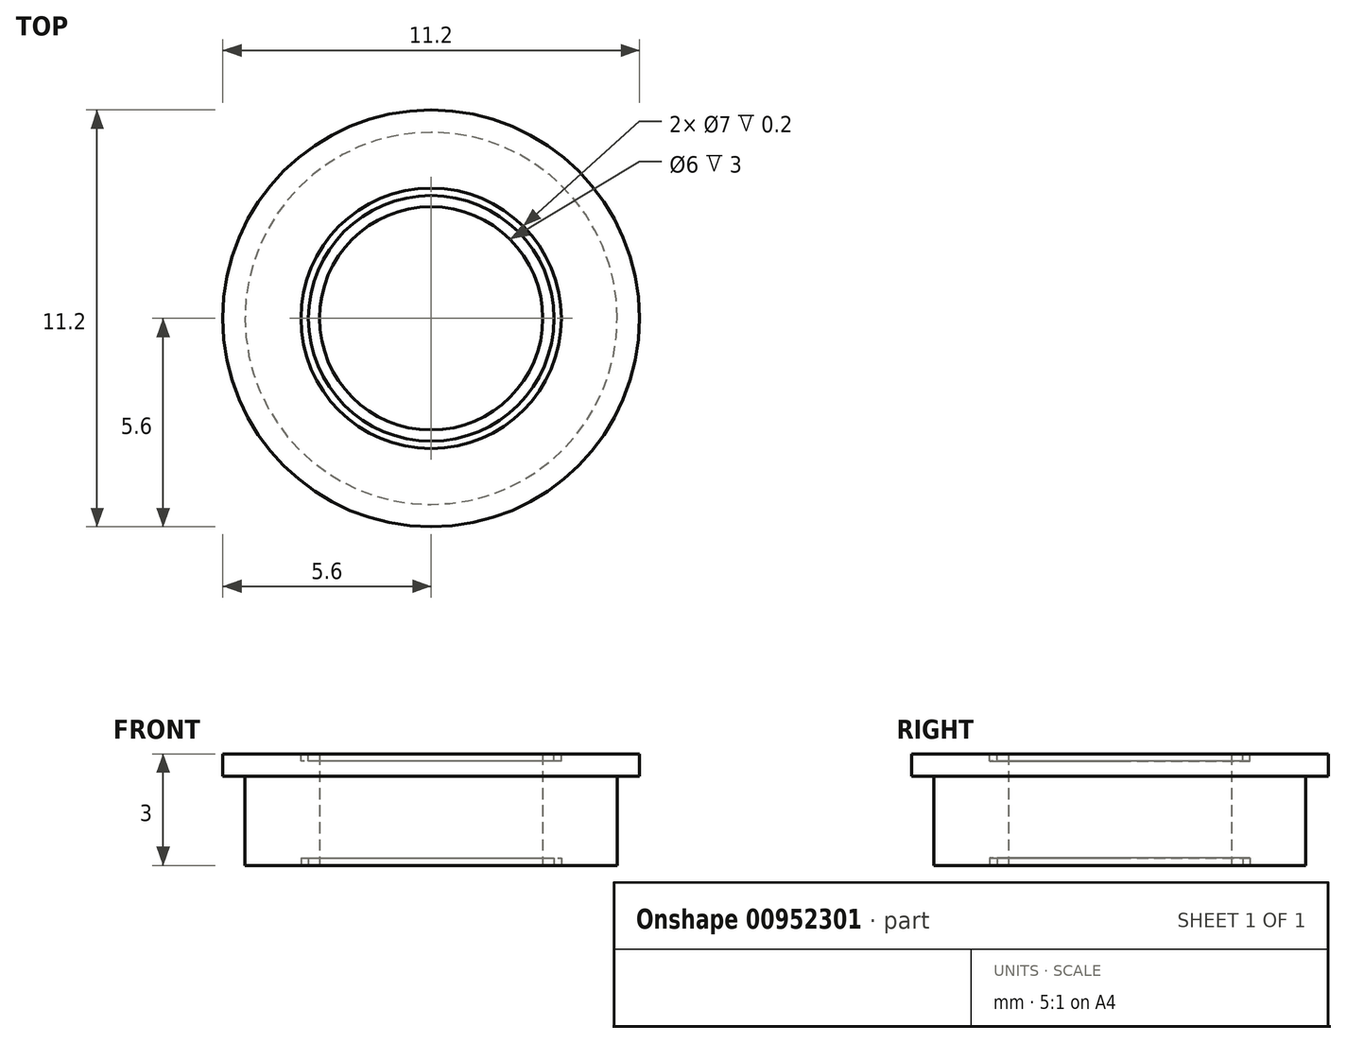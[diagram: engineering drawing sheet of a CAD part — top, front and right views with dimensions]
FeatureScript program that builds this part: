
annotation { "Feature Type Name" : "Feature", "Feature Type Description" : "" }
export const myFeature = defineFeature(function(context is Context, id is Id, definition is map)
    precondition{}
    {
        {
            var Q0;
            Q0=qCreatedBy(makeId("Top.planeOp"),FACE);
            var sketch = newSketch(context, id + "F0", { "sketchPlane" : qUnion([Q0])});
            skCircle(sketch, "E0", {"center": v(0, 0) * mm, "radius": 3 * mm});
            skCircle(sketch, "E1", {"center": v(0, 0) * mm, "radius": 5 * mm});
            skSolve(sketch);
        }
        {
            var Q0;
            Q0=qSketchRegion(id+"F0",true);
            extrude(context, id + "F1", {"entities" : qUnion([Q0]), "depth" : 3 * mm, "offsetDistance" : 25 * mm});
        }
        {
            var Q0;
            Q0=makeQuery(id+"F1.opExtrude","CAP_FACE",FACE,{"disambiguationData":[OSD([sQuery(id+"F0.wireOp",EDGE,"E0"),sQuery(id+"F0.wireOp",EDGE,"E1")])],"isStart":false});
            var sketch = newSketch(context, id + "F2", { "sketchPlane" : qUnion([Q0])});
            skCircle(sketch, "E2", {"center": v(0, 0) * mm, "radius": 5.6 * mm});
            skCircle(sketch, "E3", {"center": v(0, 0) * mm, "radius": 3.8 * mm});
            skSolve(sketch);
        }
        {
            var Q0;
            Q0=qSketchRegion(id+"F2",true);
            extrude(context, id + "F3", {"entities" : qUnion([Q0]), "operationType" : NewBodyOperationType.ADD, "oppositeDirection" : true, "depth" : 0.6 * mm, "offsetDistance" : 25 * mm});
        }
        {
            var Q0;
            Q0=makeQuery(id+"F3.boolean.opBoolean","MERGE",FACE,{"derivedFrom":[makeQuery(id+"F1.opExtrude","CAP_FACE",FACE,{"disambiguationData":[OSD([sQuery(id+"F0.wireOp",EDGE,"E0"),sQuery(id+"F0.wireOp",EDGE,"E1")])],"isStart":false}),makeQuery(id+"F3.opExtrude","CAP_FACE",FACE,{"disambiguationData":[OSD([sQuery(id+"F2.wireOp",EDGE,"E2"),sQuery(id+"F2.wireOp",EDGE,"E3")])],"isStart":true})]});
            var sketch = newSketch(context, id + "F4", { "sketchPlane" : qUnion([Q0])});
            skCircle(sketch, "E4", {"center": v(0, 0) * mm, "radius": 3.3 * mm});
            skCircle(sketch, "E5", {"center": v(0, 0) * mm, "radius": 3.5 * mm});
            skSolve(sketch);
        }
        {
            var Q0;
            Q0=qSketchRegion(id+"F4",true);
            extrude(context, id + "F5", {"entities" : qUnion([Q0]), "operationType" : NewBodyOperationType.REMOVE, "oppositeDirection" : true, "depth" : 0.2 * mm, "offsetDistance" : 25 * mm});
        }
        {
            var Q0;
            Q0=makeQuery(id+"F1.opExtrude","CAP_FACE",FACE,{"disambiguationData":[OSD([sQuery(id+"F0.wireOp",EDGE,"E0"),sQuery(id+"F0.wireOp",EDGE,"E1")])],"isStart":true});
            var sketch = newSketch(context, id + "F6", { "sketchPlane" : qUnion([Q0])});
            skCircle(sketch, "E6", {"center": v(0, 0) * mm, "radius": 3.3 * mm});
            skCircle(sketch, "E7", {"center": v(0, 0) * mm, "radius": 3.5 * mm});
            skSolve(sketch);
        }
        {
            var Q0;
            Q0=qSketchRegion(id+"F6",true);
            extrude(context, id + "F7", {"entities" : qUnion([Q0]), "operationType" : NewBodyOperationType.REMOVE, "oppositeDirection" : true, "depth" : 0.2 * mm, "offsetDistance" : 25 * mm});
        }
    });
